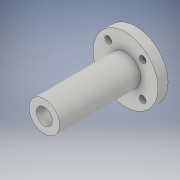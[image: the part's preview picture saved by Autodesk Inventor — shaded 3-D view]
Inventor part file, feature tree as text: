
AUTODESK INVENTOR PART (.ipt)
format: ipt  version: 2018 (Build 220112000, 112)  size: 148,992 bytes
history: native  units: in
note: dims shown in document units (in); Inventor stores cm internally (conversion verified against a paired STEP export)
features: sketch x4, extrude x3, revolve x1
ambient origin geometry x8: Origin, YZ Plane, XZ Plane, XY Plane, X Axis, Y Axis, Z Axis, Center Point
bodies: Solid1 (feature_tree)
feature tree (8):
  revolve  "Revolution1"  [1 undecoded]
  extrude  "Extrusion1"  Depth=0.6299in
  extrude  "Extrusion2"  Depth=1.7717in
  extrude  "Extrusion3"  Depth=0.1299in
  sketch  "Sketch1"  dims[d0=0.2953in d1=0.1969in]
  sketch  "Sketch2"  dims[d2=90.0deg d3=0.6299in]
  sketch  "Sketch3"  dims[d4=1.7717in d5=0.315in]
  sketch  "Sketch4"  dims[d6=0.3937in d7=0.0in d8=0.1339in d9=0.4724in d10=45.0deg d11=1.5748in d13=360.0deg d15=0.3937in d16=0.0in d17=0.2559in d18=1.5748in d20=360.0deg d22=0.1299in d23=0.0in]
note: 1 required parameter value undecoded (feature->parameter linkage not recoverable at this tier; creation-order binding heuristic only, values carry confidence <= 0.55)
